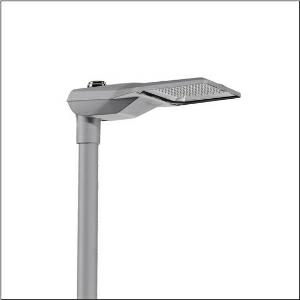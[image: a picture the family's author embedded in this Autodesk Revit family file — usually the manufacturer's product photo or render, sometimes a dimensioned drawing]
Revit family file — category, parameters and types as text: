
# Revit family: streetlight_sl_21_midi___st1_0a_5xe7d47n08lb_f0d9
name_source: partatom
category: Lighting Fixtures
units: mm (PartAtom-declared; Revit-internal decimal feet)

## family parameters
Cut with Voids When Loaded = No
Host = Face
Light Source = No
Part Type = Normal
Room Calculation Point = No
Round Connector Dimension = Use Diameter
Shared = No

## types (1)
- --- (1 x LED, 14950 lm, 98.3 W, 4000K)
    Apparent Load = 98 VA
    CIE Flux Codes = 37 72 97 100 100
    Color Rendering = 70
    Color Temperature = 4000K
    Default Elevation = 1800 mm
    Description = Streetlight SL 21 midi, mast luminaire, primary light control with lens, of PMMA, primary optical cover: cover, of toughened safety glass, transparent, light distribution: ST1.0a, light emission: direct distribution, primary light characteristic: asymmetric, installation type: side-entry, LED, 3G 2.5mm², High Power LED, rated luminous flux: 14.950lm, luminous efficacy: 152lm/W, light colour: 740, colour temperature: 4000K, control gear: NEMA (7pin), control: overheat protection, pre-setting: linear dimming characteristic, constant luminous flux control, time-dependent luminous flux control, flexible luminous flux parameterisation, mains connection: 220..240V, AC, 50/60Hz, connection cable pre-assembled, cable length: 10,5m, wiring characteristics: H05VV-F, start of lifetime: 98W, end of service life: 101W, reduction: 45W, luminaire housing, of diecast aluminium (EN AC-44300), powder-coated, Siteco® metallic grey (DB 702S), corrosivity category C5 mid according to DIN EN ISO 12944, multi-level sealing system, sealing non-destructively replaceable, inclination adjustable: 0°, 5°, 10°, 15°, length: 644mm, width: 335mm, height: 110mm, spigot size: 42mm (side-entry), mounting height: 4..8m, protection rating (complete): IP66, insulation class (complete): insulation class I (protective earthing), certification: CE, ENEC, ENEC+, VDE, impact resistance: IK09, permissible operating ambient temperature for outdoor applications: -40..+50°C, standard-compliant lighting for roads and squares, packaging unit: 1 piece

Light Distribution: ST1.0a
    Height = 111 mm
    Lamp = 1 x LED
    Lamp Light Flux = 14950 lm
    Lamp Power = 98.3 W
    Lamp count = 1
    Length = 644 mm
    Luminous efficacy = 152 lm/W
    Manufacturer = Siteco
    ModVariant = No
    Model = 5XE7D47N08LB
    Number of Poles = 1
    OnlyDefault = Yes
    Power Factor = 1
    Product Name = Streetlight SL 21 midi | ST1.0a
    Product group = mast luminaire | pylon top
    ProductGroupID = 6100
    Protection Class = Protection class I
    Protection Degree = IP 66
    RLX_Detail_Level = 1
    RLX_Emergency_Light_Flux = 0 lm
    RLX_Emergency_Type = 0
    RLX_Emergency_Type_DB = No
    RlxData = <blob elided: 90869 chars, md5=c41e50e2>
    Socket = socket
    Standby Power = 0 W
    System Light Flux = 14950 lm
    System Power = 98 W
    Type Comments = factory setting: luminous flux: 100 % | dim-lin: 254 | 1020 mA
    Type Image = l_1294377.jpg
    URL = http://relux.com
    VarID = @adj_133438
    Voltage = 0 V
    Weight = 0.00 kg
    Width = 336 mm

## geometry (parser evidence)
native form markers: Blend x4, Sweep x10
no freeform markers — native parametric forms only
